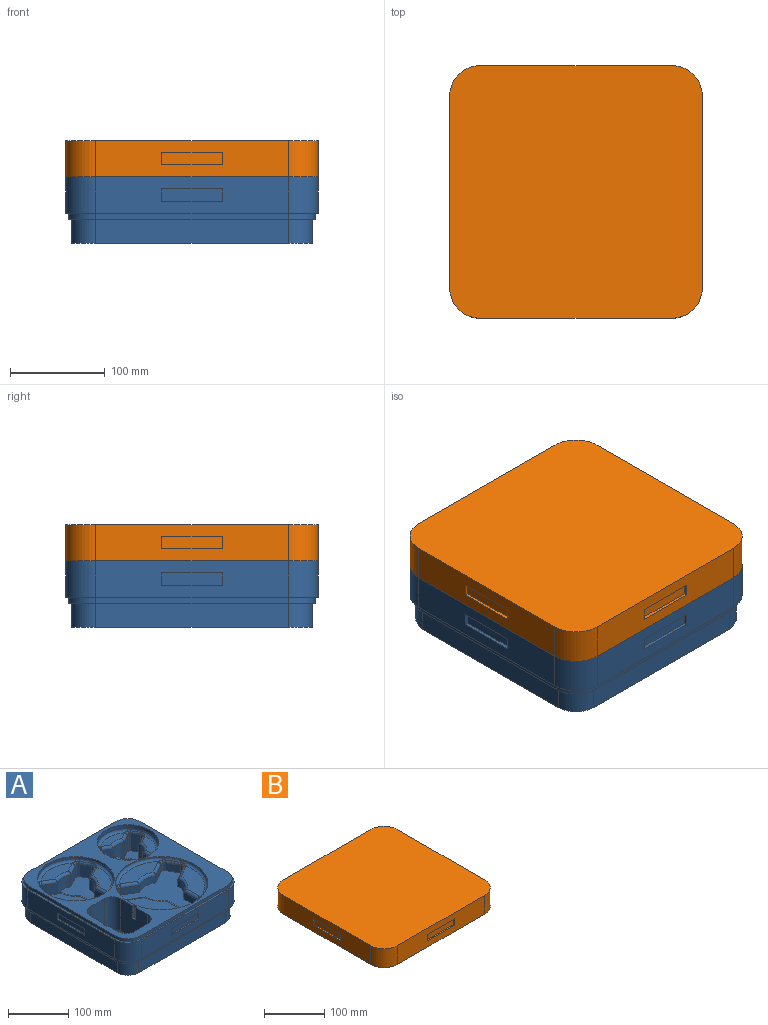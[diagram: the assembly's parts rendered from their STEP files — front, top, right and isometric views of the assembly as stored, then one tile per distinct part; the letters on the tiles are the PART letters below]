
ASSEMBLY  parts=2 mates=1
PART A: 313 faces, bbox 266.7x266.7x78.5 mm
  f0: plane 260.35x260.35mm, normal (0,0,1), area 21239.2mm2, adj f1,f17,f38,f59,f79,f80,f81,f82
  f1: plane 66.04x63.5mm, normal (-1,0,0), area 4032.2mm2, adj f0,f80,f81,f87,f309,f310,f312
  f2: plane 203.2x38.1mm, normal (1,0,0), area 6935.5mm2, adj f6,f9,f265,f274,f300,f301,f302,f303
  f3: plane 203.2x38.1mm, normal (0,1,0), area 6935.5mm2, adj f8,f9,f265,f274,f295,f296,f297,f298
  f4: plane 203.2x38.1mm, normal (-1,0,0), area 6935.5mm2, adj f7,f8,f265,f274,f290,f291,f292,f293
  f5: plane 203.2x38.1mm, normal (0,-1,0), area 6935.5mm2, adj f6,f7,f265,f274,f285,f286,f287,f288
  f6: cylinder r=31.75mm len=38.1mm, axis (0,0,1), area 1900.2mm2, adj f2,f5,f265,f274
  f7: cylinder r=31.75mm len=38.1mm, axis (0,0,1), area 1900.2mm2, adj f4,f5,f265,f274
  f8: cylinder r=31.75mm len=38.1mm, axis (0,0,1), area 1900.2mm2, adj f3,f4,f265,f274
  f9: cylinder r=31.75mm len=38.1mm, axis (0,0,1), area 1900.2mm2, adj f2,f3,f265,f274
  f10: plane 55.18x17.94mm, normal (0,0,1), area 651.1mm2, adj f131,f224,f226,f228
  f11: plane 47.78x27.94mm, normal (0,0,1), area 651.1mm2, adj f126,f229,f231,f233
  f12: plane 73.54x25.13mm, normal (0,0,1), area 1214.4mm2, adj f119,f184,f186,f188,f190,f192
  f13: plane 63.69x37.49mm, normal (0,0,1), area 1214.4mm2, adj f114,f189,f191,f193,f195,f197
  f14: plane 92.17x32.32mm, normal (0,0,1), area 1949.1mm2, adj f103,f173,f175,f176,f177,f178
  f15: plane 79.82x47.25mm, normal (0,0,1), area 1949.1mm2, adj f98,f145,f147,f149,f151,f153
  f16: plane 47.78x27.94mm, normal (0,0,1), area 651.1mm2, adj f134,f252,f254,f256
  f17: cylinder r=50.8mm len=101.6mm, axis (0,0,1), area 2476.3mm2, adj f0,f125,f126,f127,f128,f129,f130,f131
  f18: plane 91.6x80.5mm, normal (0,0,1), area 3762.4mm2, adj f19,f20,f21,f22,f23,f24,f25,f26
  f19: plane 33.06x18.21mm, normal (0.5,0.87,0), area 694.5mm2, adj f18,f20,f36,f227,f229
  f20: cylinder r=4.37mm len=35.74mm, axis (0,0,1), area 238.6mm2, adj f18,f19,f21,f219,f221,f223,f225
  f21: plane 35.69x14.43mm, normal (0.87,-0.5,0), area 590.4mm2, adj f18,f20,f22,f217
  f22: cylinder r=4.37mm len=35.74mm, axis (0,0,1), area 238.6mm2, adj f18,f21,f23,f215,f216,f218,f220
  f23: plane 33.06x18.21mm, normal (-0.5,-0.87,0), area 694.5mm2, adj f18,f22,f24,f222,f224
  f24: cylinder r=25.4mm len=33.02mm, axis (0,0,1), area 878.3mm2, adj f18,f23,f25,f226
  f25: plane 33.06x18.21mm, normal (0.5,-0.87,0), area 694.5mm2, adj f18,f24,f26,f228,f230
  f26: cylinder r=4.37mm len=35.74mm, axis (0,0,1), area 238.6mm2, adj f18,f25,f27,f232,f234,f236,f238
  f27: plane 35.7x14.44mm, normal (-0.87,-0.5,0), area 590.4mm2, adj f18,f26,f28,f240
  f28: cylinder r=4.37mm len=35.74mm, axis (0,0,1), area 238.6mm2, adj f18,f27,f29,f242,f244,f246,f248
  f29: plane 33.06x18.21mm, normal (-0.5,0.87,0), area 694.5mm2, adj f18,f28,f30,f250,f252
  f30: cylinder r=25.4mm len=33.02mm, axis (0,0,1), area 878.3mm2, adj f18,f29,f31,f254
  f31: plane 33.06x21.03mm, normal (-1,0,0), area 694.5mm2, adj f18,f30,f32,f255,f256
  f32: cylinder r=4.37mm len=35.74mm, axis (0,0,1), area 238.6mm2, adj f18,f31,f33,f247,f249,f251,f253
  f33: plane 35.69x16.66mm, normal (0,1,0), area 590.4mm2, adj f18,f32,f34,f245
  f34: cylinder r=4.37mm len=35.74mm, axis (0,0,1), area 238.6mm2, adj f18,f33,f35,f237,f239,f241,f243
  f35: plane 33.06x21.03mm, normal (1,0,0), area 694.5mm2, adj f18,f34,f36,f233,f235
  f36: cylinder r=25.4mm len=33.02mm, axis (0,0,1), area 878.3mm2, adj f18,f19,f35,f231
  f37: plane 63.69x37.49mm, normal (0,0,1), area 1214.4mm2, adj f122,f208,f210,f212,f213,f214
  f38: cylinder r=63.5mm len=127mm, axis (0,0,1), area 1800.1mm2, adj f0,f113,f114,f115,f116,f117,f118,f119
  f39: plane 114.5x100.62mm, normal (0,0,1), area 5878.8mm2, adj f40,f41,f42,f43,f44,f45,f46,f47
  f40: plane 23.5x22.77mm, normal (0.5,0.87,0), area 617.7mm2, adj f39,f41,f57,f191
  f41: cylinder r=5.46mm len=25.84mm, axis (0,0,1), area 212.8mm2, adj f39,f40,f42,f183,f185,f187,f189
  f42: plane 25.8x18.04mm, normal (0.87,-0.5,0), area 530.7mm2, adj f39,f41,f43,f181
  f43: cylinder r=5.46mm len=25.84mm, axis (0,0,1), area 212.8mm2, adj f39,f42,f44,f179,f180,f182,f184
  f44: plane 23.5x22.77mm, normal (-0.5,-0.87,0), area 617.7mm2, adj f39,f43,f45,f186
  f45: cylinder r=31.75mm len=31.75mm, axis (0,0,1), area 781.2mm2, adj f39,f44,f46,f188
  f46: plane 23.5x22.77mm, normal (0.5,-0.87,0), area 617.7mm2, adj f39,f45,f47,f190
  f47: cylinder r=5.46mm len=25.84mm, axis (0,0,1), area 212.8mm2, adj f39,f46,f48,f192,f194,f196,f198
  f48: plane 25.8x18.05mm, normal (-0.87,-0.5,0), area 530.7mm2, adj f39,f47,f49,f200
  f49: cylinder r=5.46mm len=25.84mm, axis (0,0,1), area 212.8mm2, adj f39,f48,f50,f202,f204,f206,f208
  f50: plane 23.5x22.77mm, normal (-0.5,0.87,0), area 617.7mm2, adj f39,f49,f51,f210
  f51: cylinder r=31.75mm len=27.5mm, axis (0,0,1), area 781.2mm2, adj f39,f50,f52,f212
  f52: plane 26.29x23.5mm, normal (-1,0,0), area 617.7mm2, adj f39,f51,f53,f214
  f53: cylinder r=5.46mm len=25.84mm, axis (0,0,1), area 212.8mm2, adj f39,f52,f54,f207,f209,f211,f213
  f54: plane 25.8x20.83mm, normal (0,1,0), area 530.7mm2, adj f39,f53,f55,f205
  f55: cylinder r=5.46mm len=25.84mm, axis (0,0,1), area 212.8mm2, adj f39,f54,f56,f197,f199,f201,f203
  f56: plane 26.29x23.5mm, normal (1,0,0), area 617.7mm2, adj f39,f55,f57,f195
  f57: cylinder r=31.75mm len=27.5mm, axis (0,0,1), area 781.2mm2, adj f39,f40,f56,f193
  f58: plane 79.82x47.25mm, normal (0,0,1), area 1949.1mm2, adj f110,f148,f150,f152,f154,f156
  f59: cylinder r=76.2mm len=152.4mm, axis (0,0,1), area 613.9mm2, adj f0,f95,f96,f97,f98,f99,f100,f101
  f60: plane 137.39x120.74mm, normal (0,0,1), area 8465.4mm2, adj f61,f62,f63,f64,f65,f66,f67,f68
  f61: plane 31.55x13.97mm, normal (1,0,0), area 440.7mm2, adj f60,f62,f78,f147
  f62: cylinder r=38.1mm len=33mm, axis (0,0,1), area 557.4mm2, adj f60,f61,f63,f149
  f63: plane 27.32x15.77mm, normal (0.5,0.87,0), area 440.7mm2, adj f60,f62,f64,f151
  f64: cylinder r=6.55mm len=15.95mm, axis (0,0,1), area 154.1mm2, adj f60,f63,f65,f153,f155,f157,f159
  f65: plane 21.65x15.9mm, normal (0.87,-0.5,0), area 387.7mm2, adj f60,f64,f66,f161,f163,f165
  f66: cylinder r=6.55mm len=15.95mm, axis (0,0,1), area 154.1mm2, adj f60,f65,f67,f167,f169,f171,f173
  f67: plane 27.32x15.77mm, normal (-0.5,-0.87,0), area 440.7mm2, adj f60,f66,f68,f175
  f68: cylinder r=38.1mm len=38.1mm, axis (0,0,1), area 557.4mm2, adj f60,f67,f69,f177
  f69: plane 27.32x15.77mm, normal (0.5,-0.87,0), area 440.7mm2, adj f60,f68,f70,f178
  f70: cylinder r=6.55mm len=15.95mm, axis (0,0,1), area 154.1mm2, adj f60,f69,f71,f170,f172,f174,f176
  f71: plane 21.65x15.9mm, normal (-0.87,-0.5,0), area 387.7mm2, adj f60,f70,f72,f164,f166,f168
  f72: cylinder r=6.55mm len=15.95mm, axis (0,0,1), area 154.1mm2, adj f60,f71,f73,f156,f158,f160,f162
  f73: plane 27.32x15.77mm, normal (-0.5,0.87,0), area 440.7mm2, adj f60,f72,f74,f154
  f74: cylinder r=38.1mm len=33mm, axis (0,0,1), area 557.4mm2, adj f60,f73,f75,f152
  f75: plane 31.55x13.97mm, normal (-1,0,0), area 440.7mm2, adj f60,f74,f76,f150
  f76: cylinder r=6.55mm len=15.95mm, axis (0,0,1), area 154.1mm2, adj f60,f75,f77,f142,f144,f146,f148
  f77: plane 25x15.9mm, normal (0,1,0), area 387.7mm2, adj f60,f76,f78,f137,f138,f140
  f78: cylinder r=6.55mm len=15.95mm, axis (0,0,1), area 154.1mm2, adj f60,f61,f77,f139,f141,f143,f145
  f79: plane 66.04x31.75mm, normal (0,1,0), area 2096.8mm2, adj f0,f80,f85,f91
  f80: cylinder r=19.05mm len=66.04mm, axis (0,0,1), area 1976.2mm2, adj f0,f1,f79,f89
  f81: cylinder r=19.05mm len=66.04mm, axis (0,0,1), area 1976.2mm2, adj f0,f1,f82,f88
  f82: plane 66.04x31.75mm, normal (0,-1,0), area 2096.8mm2, adj f0,f81,f83,f90
  f83: cylinder r=19.05mm len=66.04mm, axis (0,0,1), area 1976.2mm2, adj f0,f82,f84,f92
  f84: plane 66.04x63.5mm, normal (1,0,0), area 4032.3mm2, adj f0,f83,f85,f94,f305,f307,f308
  f85: cylinder r=19.05mm len=66.04mm, axis (0,0,1), area 1976.2mm2, adj f0,f79,f84,f93
  f86: plane 91.44x59.69mm, normal (0,0,1), area 5290.5mm2, adj f87,f88,f89,f90,f91,f92,f93,f94
  f87: cylinder r=5.08mm len=63.5mm, axis (0,1,0), area 506.7mm2, adj f1,f86,f88,f89
  f88: torus R=13.97mm, axis (0,0,1), area 215.6mm2, adj f81,f86,f87,f90
  f89: torus R=13.97mm, axis (0,0,1), area 215.6mm2, adj f80,f86,f87,f91
  f90: cylinder r=5.08mm len=31.75mm, axis (-1,0,0), area 253.4mm2, adj f82,f86,f88,f92
  f91: cylinder r=5.08mm len=31.75mm, axis (1,0,0), area 253.4mm2, adj f79,f86,f89,f93
  f92: torus R=13.97mm, axis (0,0,1), area 215.6mm2, adj f83,f86,f90,f94
  f93: torus R=13.97mm, axis (0,0,1), area 215.6mm2, adj f85,f86,f91,f94
  f94: cylinder r=5.08mm len=63.5mm, axis (0,-1,0), area 506.7mm2, adj f84,f86,f92,f93
  f95: bspline ~17.19x11.79mm, area 57.1mm2, adj f59,f96,f97,f159,f161
  f96: bspline ~7.71x6.01mm, area 24.7mm2, adj f59,f95,f98,f157
  f97: torus R=71.12mm, axis (0,0,1), area 21mm2, adj f59,f95,f99,f163
  f98: torus R=71.12mm, axis (0,0,1), area 930.2mm2, adj f15,f59,f96,f100,f143,f155
  f99: bspline ~14.9x11.49mm, area 57.1mm2, adj f59,f97,f101,f165,f167
  f100: bspline ~7.36x6.51mm, area 24.7mm2, adj f59,f98,f102,f141
  f101: bspline ~8.2x7.73mm, area 24.7mm2, adj f59,f99,f103,f169
  f102: bspline ~15.1x5.11mm, area 57.1mm2, adj f59,f100,f104,f137,f139
  f103: torus R=71.12mm, axis (0,0,1), area 930.2mm2, adj f14,f59,f101,f105,f171,f174
  f104: torus R=71.12mm, axis (0,0,1), area 21mm2, adj f59,f102,f106,f138
  f105: bspline ~8.27x7.77mm, area 24.7mm2, adj f59,f103,f107,f172
  f106: bspline ~18.01x5.11mm, area 57.1mm2, adj f59,f104,f108,f140,f142
  f107: bspline ~17.15x12.87mm, area 57.1mm2, adj f59,f105,f109,f168,f170
  f108: bspline ~7.45x6.62mm, area 24.7mm2, adj f59,f106,f110,f144
  f109: torus R=71.12mm, axis (0,0,1), area 21mm2, adj f59,f107,f111,f166
  f110: torus R=71.12mm, axis (0,0,1), area 930.2mm2, adj f58,f59,f108,f112,f146,f158
  f111: bspline ~14.79x10.74mm, area 57.1mm2, adj f59,f109,f112,f162,f164
  f112: bspline ~7.69x6.02mm, area 24.7mm2, adj f59,f110,f111,f160
  f113: bspline ~7.36x5.26mm, area 23.2mm2, adj f38,f114,f115,f185
  f114: torus R=58.42mm, axis (0,0,1), area 751.7mm2, adj f13,f38,f113,f116,f187,f199
  f115: bspline ~23.49x15.24mm, area 103.3mm2, adj f38,f113,f117,f179,f181,f183
  f116: bspline ~7.62x6.6mm, area 23.2mm2, adj f38,f114,f118,f201
  f117: bspline ~8.28x7.58mm, area 23.2mm2, adj f38,f115,f119,f180
  f118: bspline ~26.54x5.01mm, area 103.3mm2, adj f38,f116,f120,f203,f205,f207
  f119: torus R=58.42mm, axis (0,0,1), area 751.7mm2, adj f12,f38,f117,f121,f182,f194
  f120: bspline ~7.09x6.44mm, area 23.2mm2, adj f38,f118,f122,f209
  f121: bspline ~7.97x7.13mm, area 23.2mm2, adj f38,f119,f123,f196
  f122: torus R=58.42mm, axis (0,0,1), area 751.7mm2, adj f37,f38,f120,f124,f206,f211
  f123: bspline ~23.5x15.19mm, area 103.3mm2, adj f38,f121,f124,f198,f200,f202
  f124: bspline ~7.75x5.51mm, area 23.2mm2, adj f38,f122,f123,f204
  f125: bspline ~6.65x5.33mm, area 20.4mm2, adj f17,f126,f127,f221,f223
  f126: torus R=45.72mm, axis (0,0,1), area 575.4mm2, adj f11,f17,f125,f128,f225,f227,f235,f237
  f127: bspline ~18.49x12.09mm, area 74.2mm2, adj f17,f125,f129,f215,f217,f219
  f128: bspline ~6.77x6.31mm, area 20.4mm2, adj f17,f126,f130,f239,f241
  f129: bspline ~7.62x6.56mm, area 20.4mm2, adj f17,f127,f131,f216,f218
  f130: bspline ~21.1x4.8mm, area 74.2mm2, adj f17,f128,f132,f243,f245,f247
  f131: torus R=45.72mm, axis (0,0,1), area 575.4mm2, adj f10,f17,f129,f133,f220,f222,f230,f232
  f132: bspline ~6.73x6.38mm, area 20.4mm2, adj f17,f130,f134,f249,f251
  f133: bspline ~7.53x6.45mm, area 20.4mm2, adj f17,f131,f135,f234,f236
  f134: torus R=45.72mm, axis (0,0,1), area 575.4mm2, adj f16,f17,f132,f136,f248,f250,f253,f255
  f135: bspline ~18.52x11.93mm, area 74.2mm2, adj f17,f133,f136,f238,f240,f242
  f136: bspline ~6.88x5.21mm, area 20.4mm2, adj f17,f134,f135,f244,f246
  f137: bspline ~14.38x4.67mm, area 52.8mm2, adj f77,f102,f138,f139
  f138: bspline ~9x4.47mm, area 20.9mm2, adj f77,f104,f137,f140
  f139: bspline ~4.3x3.11mm, area 2.8mm2, adj f78,f102,f137,f141
  f140: bspline ~16.91x4.74mm, area 52.8mm2, adj f77,f106,f138,f142
  f141: bspline ~5.18x4.35mm, area 19.7mm2, adj f78,f100,f139,f143
  f142: bspline ~4.51x4.47mm, area 2.8mm2, adj f76,f106,f140,f144
  f143: bspline ~9.19x6.77mm, area 38.2mm2, adj f78,f98,f141,f145
  f144: bspline ~5.97x4.39mm, area 19.8mm2, adj f76,f108,f142,f146
  f145: torus R=11.63mm, axis (0,0,1), area 14.2mm2, adj f15,f78,f143,f147
  f146: bspline ~9.56x7.54mm, area 38.2mm2, adj f76,f110,f144,f148
  f147: cylinder r=5.08mm len=31.55mm, axis (0,-1,0), area 240.5mm2, adj f15,f61,f145,f149
  f148: torus R=11.63mm, axis (0,0,1), area 14.2mm2, adj f58,f76,f146,f150
  f149: torus R=43.18mm, axis (0,0,1), area 311.2mm2, adj f15,f62,f147,f151
  f150: cylinder r=5.08mm len=31.55mm, axis (0,1,0), area 240.5mm2, adj f58,f75,f148,f152
  f151: cylinder r=5.08mm len=29.86mm, axis (0.87,-0.5,0), area 240.5mm2, adj f15,f63,f149,f153
  f152: torus R=43.18mm, axis (0,0,1), area 311.2mm2, adj f58,f74,f150,f154
  f153: torus R=11.63mm, axis (0,0,1), area 14.2mm2, adj f15,f64,f151,f155
  f154: cylinder r=5.08mm len=29.86mm, axis (0.87,0.5,0), area 240.5mm2, adj f58,f73,f152,f156
  f155: bspline ~10.65x6.1mm, area 38.2mm2, adj f64,f98,f153,f157
  f156: torus R=11.63mm, axis (0,0,1), area 14.2mm2, adj f58,f72,f154,f158
  f157: bspline ~5.95x4.39mm, area 19.8mm2, adj f64,f96,f155,f159
  f158: bspline ~10.65x6.1mm, area 38.2mm2, adj f72,f110,f156,f160
  f159: bspline ~4.66x4.47mm, area 2.8mm2, adj f64,f95,f157,f161
  f160: bspline ~5.96x4.39mm, area 19.8mm2, adj f72,f112,f158,f162
  f161: bspline ~15.88x9.79mm, area 52.8mm2, adj f65,f95,f159,f163
  f162: bspline ~4.3x3.27mm, area 2.8mm2, adj f72,f111,f160,f164
  f163: bspline ~11.44x8.02mm, area 20.9mm2, adj f65,f97,f161,f165
  f164: bspline ~13.69x8.75mm, area 52.8mm2, adj f71,f111,f162,f166
  f165: bspline ~13.13x9.38mm, area 52.8mm2, adj f65,f99,f163,f167
  f166: bspline ~11.44x8.02mm, area 20.9mm2, adj f71,f109,f164,f168
  f167: bspline ~4.3x3.32mm, area 2.8mm2, adj f66,f99,f165,f169
  f168: bspline ~15.16x10.64mm, area 52.8mm2, adj f71,f107,f166,f170
  f169: bspline ~4.78x4.64mm, area 19.7mm2, adj f66,f101,f167,f171
  f170: bspline ~4.47x4.22mm, area 2.8mm2, adj f70,f107,f168,f172
  f171: bspline ~8.96x6.1mm, area 38.2mm2, adj f66,f103,f169,f173
  f172: bspline ~5.34x5.17mm, area 19.8mm2, adj f70,f105,f170,f174
  f173: torus R=11.63mm, axis (0,0,1), area 14.2mm2, adj f14,f66,f171,f175
  f174: bspline ~9.83x6.1mm, area 38.2mm2, adj f70,f103,f172,f176
  f175: cylinder r=5.08mm len=29.86mm, axis (-0.87,0.5,0), area 240.5mm2, adj f14,f67,f173,f177
  f176: torus R=11.63mm, axis (0,0,1), area 14.2mm2, adj f14,f70,f174,f178
  f177: torus R=43.18mm, axis (0,0,1), area 311.2mm2, adj f14,f68,f175,f178
  f178: cylinder r=5.08mm len=29.86mm, axis (-0.87,-0.5,0), area 240.5mm2, adj f14,f69,f176,f177
  f179: bspline ~4x2.81mm, area 2.3mm2, adj f43,f115,f180,f181
  f180: bspline ~4.8x4.71mm, area 18.3mm2, adj f43,f117,f179,f182
  f181: bspline ~20.94x13.01mm, area 95.3mm2, adj f42,f115,f179,f183
  f182: bspline ~9.08x6.3mm, area 34.2mm2, adj f43,f119,f180,f184
  f183: bspline ~4.17x3.97mm, area 2.3mm2, adj f41,f115,f181,f185
  f184: torus R=10.54mm, axis (0,0,1), area 4.2mm2, adj f12,f43,f182,f186
  f185: bspline ~5.81x4.17mm, area 18.3mm2, adj f41,f113,f183,f187
  f186: cylinder r=5.08mm len=25.31mm, axis (-0.87,0.5,0), area 198.6mm2, adj f12,f44,f184,f188
  f187: bspline ~9.84x6.3mm, area 34.2mm2, adj f41,f114,f185,f189
  f188: torus R=36.83mm, axis (0,0,1), area 258.3mm2, adj f12,f45,f186,f190
  f189: torus R=10.54mm, axis (0,0,1), area 4.2mm2, adj f13,f41,f187,f191
  f190: cylinder r=5.08mm len=25.31mm, axis (-0.87,-0.5,0), area 198.6mm2, adj f12,f46,f188,f192
  f191: cylinder r=5.08mm len=25.31mm, axis (0.87,-0.5,0), area 198.6mm2, adj f13,f40,f189,f193
  f192: torus R=10.54mm, axis (0,0,1), area 4.2mm2, adj f12,f47,f190,f194
  f193: torus R=36.83mm, axis (0,0,1), area 258.3mm2, adj f13,f57,f191,f195
  f194: bspline ~9.08x6.3mm, area 34.2mm2, adj f47,f119,f192,f196
  f195: cylinder r=5.08mm len=26.29mm, axis (0,-1,0), area 198.6mm2, adj f13,f56,f193,f197
  f196: bspline ~4.94x4.84mm, area 18.3mm2, adj f47,f121,f194,f198
  f197: torus R=10.54mm, axis (0,0,1), area 4.2mm2, adj f13,f55,f195,f199
  f198: bspline ~4.17x3.53mm, area 2.3mm2, adj f47,f123,f196,f200
  f199: bspline ~8.21x6.3mm, area 34.2mm2, adj f55,f114,f197,f201
  f200: bspline ~21.8x13.42mm, area 95.3mm2, adj f48,f123,f198,f202
  f201: bspline ~5.65x4.16mm, area 18.3mm2, adj f55,f116,f199,f203
  f202: bspline ~4x3.03mm, area 2.3mm2, adj f49,f123,f200,f204
  f203: bspline ~4x2.24mm, area 2.3mm2, adj f55,f118,f201,f205
  f204: bspline ~5.73x4.16mm, area 18.3mm2, adj f49,f124,f202,f206
  f205: bspline ~23.64x4.29mm, area 95.3mm2, adj f54,f118,f203,f207
  f206: bspline ~9.31x6.3mm, area 34.2mm2, adj f49,f122,f204,f208
  f207: bspline ~4.17x3.85mm, area 2.3mm2, adj f53,f118,f205,f209
  f208: torus R=10.54mm, axis (0,0,1), area 4.2mm2, adj f37,f49,f206,f210
  f209: bspline ~5.73x4.17mm, area 18.3mm2, adj f53,f120,f207,f211
  f210: cylinder r=5.08mm len=25.31mm, axis (0.87,0.5,0), area 198.6mm2, adj f37,f50,f208,f212
  f211: bspline ~8.4x6.77mm, area 34.2mm2, adj f53,f122,f209,f213
  f212: torus R=36.83mm, axis (0,0,1), area 258.3mm2, adj f37,f51,f210,f214
  f213: torus R=10.54mm, axis (0,0,1), area 4.2mm2, adj f37,f53,f211,f214
  f214: cylinder r=5.08mm len=26.29mm, axis (0,1,0), area 198.6mm2, adj f37,f52,f212,f213
  f215: bspline ~3.6x2.36mm, area 1.9mm2, adj f22,f127,f216,f217
  f216: bspline ~4.17x4.11mm, area 13.7mm2, adj f22,f129,f215,f218
  f217: bspline ~18.95x11.73mm, area 67.5mm2, adj f21,f127,f215,f219
  f218: bspline ~3.89x2.42mm, area 1.2mm2, adj f22,f129,f216,f220
  f219: bspline ~3.6x2.65mm, area 1.9mm2, adj f20,f127,f217,f221
  f220: bspline ~7.81x6.47mm, area 28.9mm2, adj f22,f131,f218,f222
  f221: bspline ~5.04x3.84mm, area 13.5mm2, adj f20,f125,f219,f223
  f222: bspline ~5.99x5.69mm, area 5.2mm2, adj f23,f131,f220,f224
  f223: bspline ~3.89x1.84mm, area 1.4mm2, adj f20,f125,f221,f225
  f224: cylinder r=5.08mm len=19.97mm, axis (-0.87,0.5,0), area 149.6mm2, adj f10,f23,f222,f226
  f225: bspline ~8.2x6.46mm, area 28.9mm2, adj f20,f126,f223,f227
  f226: torus R=30.48mm, axis (0,0,1), area 205.4mm2, adj f10,f24,f224,f228
  f227: bspline ~5.91x5.49mm, area 5.2mm2, adj f19,f126,f225,f229
  f228: cylinder r=5.08mm len=19.97mm, axis (-0.87,-0.5,0), area 149.6mm2, adj f10,f25,f226,f230
  f229: cylinder r=5.08mm len=19.97mm, axis (0.87,-0.5,0), area 149.6mm2, adj f11,f19,f227,f231
  f230: bspline ~5.99x5.69mm, area 5.2mm2, adj f25,f131,f228,f232
  f231: torus R=30.48mm, axis (0,0,1), area 205.4mm2, adj f11,f36,f229,f233
  f232: bspline ~7.81x6.47mm, area 28.9mm2, adj f26,f131,f230,f234
  f233: cylinder r=5.08mm len=20.12mm, axis (0,-1,0), area 149.6mm2, adj f11,f35,f231,f235
  f234: bspline ~3.89x2.43mm, area 1.4mm2, adj f26,f133,f232,f236
  f235: bspline ~5.49x5.43mm, area 5.2mm2, adj f35,f126,f233,f237
  f236: bspline ~4.14x4.09mm, area 13.5mm2, adj f26,f133,f234,f238
  f237: bspline ~6.97x6.46mm, area 28.9mm2, adj f34,f126,f235,f239
  f238: bspline ~3.82x3.04mm, area 1.9mm2, adj f26,f135,f236,f240
  f239: bspline ~3.89x2.39mm, area 1.2mm2, adj f34,f128,f237,f241
  f240: bspline ~17.63x10.89mm, area 67.5mm2, adj f27,f135,f238,f242
  f241: bspline ~4.71x3.85mm, area 13.7mm2, adj f34,f128,f239,f243
  f242: bspline ~3.82x3.38mm, area 1.9mm2, adj f28,f135,f240,f244
  f243: bspline ~3.6x2.44mm, area 1.9mm2, adj f34,f130,f241,f245
  f244: bspline ~4.84x3.85mm, area 13.7mm2, adj f28,f136,f242,f246
  f245: bspline ~21.71x3.85mm, area 67.5mm2, adj f33,f130,f243,f247
  f246: bspline ~3.89x1.84mm, area 1.2mm2, adj f28,f136,f244,f248
  f247: bspline ~3.6x2.53mm, area 1.9mm2, adj f32,f130,f245,f249
  f248: bspline ~8.2x6.46mm, area 28.9mm2, adj f28,f134,f246,f250
  f249: bspline ~4.96x3.83mm, area 13.5mm2, adj f32,f132,f247,f251
  f250: bspline ~5.91x5.49mm, area 5.2mm2, adj f29,f134,f248,f252
  f251: bspline ~3.89x2.4mm, area 1.4mm2, adj f32,f132,f249,f253
  f252: cylinder r=5.08mm len=19.97mm, axis (0.87,0.5,0), area 149.6mm2, adj f16,f29,f250,f254
  f253: bspline ~6.97x6.46mm, area 28.9mm2, adj f32,f134,f251,f255
  f254: torus R=30.48mm, axis (0,0,1), area 205.4mm2, adj f16,f30,f252,f256
  f255: bspline ~5.49x5.43mm, area 5.2mm2, adj f31,f134,f253,f256
  f256: cylinder r=5.08mm len=20.12mm, axis (0,1,0), area 149.6mm2, adj f16,f31,f254,f255
  f257: cylinder r=28.57mm len=28.58mm, axis (0,0,1), area 285mm2, adj f0,f258,f264,f265
  f258: plane 203.2x6.35mm, normal (-1,0,0), area 1290.3mm2, adj f0,f257,f259,f265
  f259: cylinder r=28.57mm len=28.58mm, axis (0,0,1), area 285mm2, adj f0,f258,f260,f265
  f260: plane 203.2x6.35mm, normal (0,1,0), area 1290.3mm2, adj f0,f259,f261,f265
  f261: cylinder r=28.57mm len=28.58mm, axis (0,0,1), area 285mm2, adj f0,f260,f262,f265
  f262: plane 203.2x6.35mm, normal (1,0,0), area 1290.3mm2, adj f0,f261,f263,f265
  f263: cylinder r=28.57mm len=28.58mm, axis (0,0,1), area 285mm2, adj f0,f262,f264,f265
  f264: plane 203.2x6.35mm, normal (0,-1,0), area 1290.3mm2, adj f0,f257,f263,f265
  f265: plane 266.7x266.7mm, normal (0,0,1), area 3182.4mm2, adj f2,f3,f4,f5,f6,f7,f8,f9
  f266: plane 203.2x6.35mm, normal (0,-1,0), area 1290.3mm2, adj f267,f273,f274,f284
  f267: cylinder r=28.57mm len=28.58mm, axis (0,0,-1), area 285mm2, adj f266,f268,f274,f284
  f268: plane 203.2x6.35mm, normal (1,0,0), area 1290.3mm2, adj f267,f269,f274,f284
  f269: cylinder r=28.57mm len=28.58mm, axis (0,0,-1), area 285mm2, adj f268,f270,f274,f284
  f270: plane 203.2x6.35mm, normal (0,1,0), area 1290.3mm2, adj f269,f271,f274,f284
  f271: cylinder r=28.57mm len=28.58mm, axis (0,0,-1), area 285mm2, adj f270,f272,f274,f284
  f272: plane 203.2x6.35mm, normal (-1,0,0), area 1290.3mm2, adj f271,f273,f274,f284
  f273: cylinder r=28.57mm len=28.58mm, axis (0,0,-1), area 285mm2, adj f266,f272,f274,f284
  f274: plane 266.7x266.7mm, normal (0,0,-1), area 3182.4mm2, adj f2,f3,f4,f5,f6,f7,f8,f9
  f275: plane 254x254mm, normal (0,0,-1), area 63962.2mm2, adj f276,f277,f278,f279,f280,f281,f282,f283
  f276: plane 203.2x25.4mm, normal (-1,0,0), area 5161.3mm2, adj f275,f277,f283,f284
  f277: cylinder r=25.4mm len=25.4mm, axis (0,0,-1), area 1013.4mm2, adj f275,f276,f278,f284
  f278: plane 203.2x25.4mm, normal (0,1,0), area 5161.3mm2, adj f275,f277,f279,f284
  f279: cylinder r=25.4mm len=25.4mm, axis (0,0,-1), area 1013.4mm2, adj f275,f278,f280,f284
  f280: plane 203.2x25.4mm, normal (1,0,0), area 5161.3mm2, adj f275,f279,f281,f284
  f281: cylinder r=25.4mm len=25.4mm, axis (0,0,-1), area 1013.4mm2, adj f275,f280,f282,f284
  f282: plane 203.2x25.4mm, normal (0,-1,0), area 5161.3mm2, adj f275,f281,f283,f284
  f283: cylinder r=25.4mm len=25.4mm, axis (0,0,-1), area 1013.4mm2, adj f275,f276,f282,f284
  f284: plane 260.35x260.35mm, normal (0,0,-1), area 3119mm2, adj f266,f267,f268,f269,f270,f271,f272,f273
  f285: plane 63.5x3.18mm, normal (0,0,1), area 201.6mm2, adj f5,f286,f288,f289
  f286: plane 12.7x3.18mm, normal (-1,0,0), area 40.3mm2, adj f5,f285,f287,f289
  f287: plane 63.5x3.18mm, normal (0,0,-1), area 201.6mm2, adj f5,f286,f288,f289
  f288: plane 12.7x3.18mm, normal (1,0,0), area 40.3mm2, adj f5,f285,f287,f289
  f289: plane 63.5x12.7mm, normal (0,-1,0), area 806.4mm2, adj f285,f286,f287,f288
  f290: plane 12.7x3.18mm, normal (0,1,0), area 40.3mm2, adj f4,f291,f293,f294
  f291: plane 63.5x3.18mm, normal (0,0,-1), area 201.6mm2, adj f4,f290,f292,f294
  f292: plane 12.7x3.18mm, normal (0,-1,0), area 40.3mm2, adj f4,f291,f293,f294
  f293: plane 63.5x3.18mm, normal (0,0,1), area 201.6mm2, adj f4,f290,f292,f294
  f294: plane 63.5x12.7mm, normal (-1,0,0), area 806.4mm2, adj f290,f291,f292,f293
  f295: plane 12.7x3.18mm, normal (1,0,0), area 40.3mm2, adj f3,f296,f298,f299
  f296: plane 63.5x3.18mm, normal (0,0,-1), area 201.6mm2, adj f3,f295,f297,f299
  f297: plane 12.7x3.18mm, normal (-1,0,0), area 40.3mm2, adj f3,f296,f298,f299
  f298: plane 63.5x3.18mm, normal (0,0,1), area 201.6mm2, adj f3,f295,f297,f299
  f299: plane 63.5x12.7mm, normal (0,1,0), area 806.5mm2, adj f295,f296,f297,f298
  f300: plane 12.7x3.18mm, normal (0,-1,0), area 40.3mm2, adj f2,f301,f303,f304
  f301: plane 63.5x3.18mm, normal (0,0,-1), area 201.6mm2, adj f2,f300,f302,f304
  f302: plane 12.7x3.18mm, normal (0,1,0), area 40.3mm2, adj f2,f301,f303,f304
  f303: plane 63.5x3.18mm, normal (0,0,1), area 201.6mm2, adj f2,f300,f302,f304
  f304: plane 63.5x12.7mm, normal (1,0,0), area 806.4mm2, adj f300,f301,f302,f303
  f305: plane 25.4x3.18mm, normal (0,-1,0), area 80.6mm2, adj f0,f84,f306,f308
  f306: plane 25.4x6.35mm, normal (1,0,0), area 161.3mm2, adj f0,f305,f307,f308
  f307: plane 25.4x3.18mm, normal (0,1,0), area 80.6mm2, adj f0,f84,f306,f308
  f308: plane 6.35x3.18mm, normal (0,0,1), area 20.2mm2, adj f84,f305,f306,f307
  f309: plane 25.4x3.18mm, normal (0,-1,0), area 80.6mm2, adj f0,f1,f311,f312
  f310: plane 25.4x3.18mm, normal (0,1,0), area 80.6mm2, adj f0,f1,f311,f312
  f311: plane 25.4x6.35mm, normal (-1,0,0), area 161.3mm2, adj f0,f309,f310,f312
  f312: plane 6.35x3.18mm, normal (0,0,1), area 20.2mm2, adj f1,f309,f310,f311
PART B: 48 faces, bbox 266.7x266.7x38.1 mm
  f0: plane 203.2x38.1mm, normal (1,0,0), area 6935.5mm2, adj f22,f23,f25,f26,f43,f44,f45,f46
  f1: plane 203.2x38.1mm, normal (0,1,0), area 6935.5mm2, adj f22,f23,f26,f27,f38,f39,f40,f41
  f2: plane 203.2x38.1mm, normal (-1,0,0), area 6935.5mm2, adj f22,f23,f24,f27,f33,f34,f35,f36
  f3: plane 203.2x38.1mm, normal (0,-1,0), area 6935.5mm2, adj f22,f23,f24,f25,f28,f29,f30,f31
  f4: plane 260.35x260.35mm, normal (0,0,-1), area 3119mm2, adj f5,f6,f7,f8,f9,f10,f11,f12
  f5: plane 203.2x25.4mm, normal (0,1,0), area 5161.3mm2, adj f4,f6,f12,f13
  f6: cylinder r=25.4mm len=25.4mm, axis (0,0,-1), area 1013.4mm2, adj f4,f5,f7,f13
  f7: plane 203.2x25.4mm, normal (1,0,0), area 5161.3mm2, adj f4,f6,f8,f13
  f8: cylinder r=25.4mm len=25.4mm, axis (0,0,-1), area 1013.4mm2, adj f4,f7,f9,f13
  f9: plane 203.2x25.4mm, normal (0,-1,0), area 5161.3mm2, adj f4,f8,f10,f13
  f10: cylinder r=25.4mm len=25.4mm, axis (0,0,-1), area 1013.4mm2, adj f4,f9,f11,f13
  f11: plane 203.2x25.4mm, normal (-1,0,0), area 5161.3mm2, adj f4,f10,f12,f13
  f12: cylinder r=25.4mm len=25.4mm, axis (0,0,-1), area 1013.4mm2, adj f4,f5,f11,f13
  f13: plane 254x254mm, normal (0,0,-1), area 63962.2mm2, adj f5,f6,f7,f8,f9,f10,f11,f12
  f14: cylinder r=28.57mm len=28.58mm, axis (0,0,1), area 285mm2, adj f4,f15,f21,f22
  f15: plane 203.2x6.35mm, normal (0,1,0), area 1290.3mm2, adj f4,f14,f16,f22
  f16: cylinder r=28.57mm len=28.58mm, axis (0,0,1), area 285mm2, adj f4,f15,f17,f22
  f17: plane 203.2x6.35mm, normal (-1,0,0), area 1290.3mm2, adj f4,f16,f18,f22
  f18: cylinder r=28.57mm len=28.58mm, axis (0,0,1), area 285mm2, adj f4,f17,f19,f22
  f19: plane 203.2x6.35mm, normal (0,-1,0), area 1290.3mm2, adj f4,f18,f20,f22
  f20: cylinder r=28.57mm len=28.58mm, axis (0,0,1), area 285mm2, adj f4,f19,f21,f22
  f21: plane 203.2x6.35mm, normal (1,0,0), area 1290.3mm2, adj f4,f14,f20,f22
  f22: plane 266.7x266.7mm, normal (0,0,-1), area 3182.4mm2, adj f0,f1,f2,f3,f14,f15,f16,f17
  f23: plane 266.7x266.7mm, normal (0,0,1), area 70263.6mm2, adj f0,f1,f2,f3,f24,f25,f26,f27
  f24: cylinder r=31.75mm len=38.1mm, axis (0,0,-1), area 1900.2mm2, adj f2,f3,f22,f23
  f25: cylinder r=31.75mm len=38.1mm, axis (0,0,-1), area 1900.2mm2, adj f0,f3,f22,f23
  f26: cylinder r=31.75mm len=38.1mm, axis (0,0,-1), area 1900.2mm2, adj f0,f1,f22,f23
  f27: cylinder r=31.75mm len=38.1mm, axis (0,0,-1), area 1900.2mm2, adj f1,f2,f22,f23
  f28: plane 12.7x3.18mm, normal (-1,0,0), area 40.3mm2, adj f3,f29,f31,f32
  f29: plane 63.5x3.18mm, normal (0,0,-1), area 201.6mm2, adj f3,f28,f30,f32
  f30: plane 12.7x3.18mm, normal (1,0,0), area 40.3mm2, adj f3,f29,f31,f32
  f31: plane 63.5x3.18mm, normal (0,0,1), area 201.6mm2, adj f3,f28,f30,f32
  f32: plane 63.5x12.7mm, normal (0,-1,0), area 806.4mm2, adj f28,f29,f30,f31
  f33: plane 12.7x3.18mm, normal (0,1,0), area 40.3mm2, adj f2,f34,f36,f37
  f34: plane 63.5x3.18mm, normal (0,0,-1), area 201.6mm2, adj f2,f33,f35,f37
  f35: plane 12.7x3.18mm, normal (0,-1,0), area 40.3mm2, adj f2,f34,f36,f37
  f36: plane 63.5x3.18mm, normal (0,0,1), area 201.6mm2, adj f2,f33,f35,f37
  f37: plane 63.5x12.7mm, normal (-1,0,0), area 806.4mm2, adj f33,f34,f35,f36
  f38: plane 12.7x3.18mm, normal (1,0,0), area 40.3mm2, adj f1,f39,f41,f42
  f39: plane 63.5x3.18mm, normal (0,0,-1), area 201.6mm2, adj f1,f38,f40,f42
  f40: plane 12.7x3.18mm, normal (-1,0,0), area 40.3mm2, adj f1,f39,f41,f42
  f41: plane 63.5x3.18mm, normal (0,0,1), area 201.6mm2, adj f1,f38,f40,f42
  f42: plane 63.5x12.7mm, normal (0,1,0), area 806.4mm2, adj f38,f39,f40,f41
  f43: plane 12.7x3.18mm, normal (0,-1,0), area 40.3mm2, adj f0,f44,f46,f47
  f44: plane 63.5x3.18mm, normal (0,0,-1), area 201.6mm2, adj f0,f43,f45,f47
  f45: plane 12.7x3.18mm, normal (0,1,0), area 40.3mm2, adj f0,f44,f46,f47
  f46: plane 63.5x3.18mm, normal (0,0,1), area 201.6mm2, adj f0,f43,f45,f47
  f47: plane 63.5x12.7mm, normal (1,0,0), area 806.4mm2, adj f43,f44,f45,f46
PLACE A t=(-1.21,45.75,-3.35)mm
PLACE B t=(-1.21,45.75,-193.85)mm
MATE fastened B.f22 <-> A.f265  axis (0,0,-1) through (-134.56,45.75,-9.7)mm
